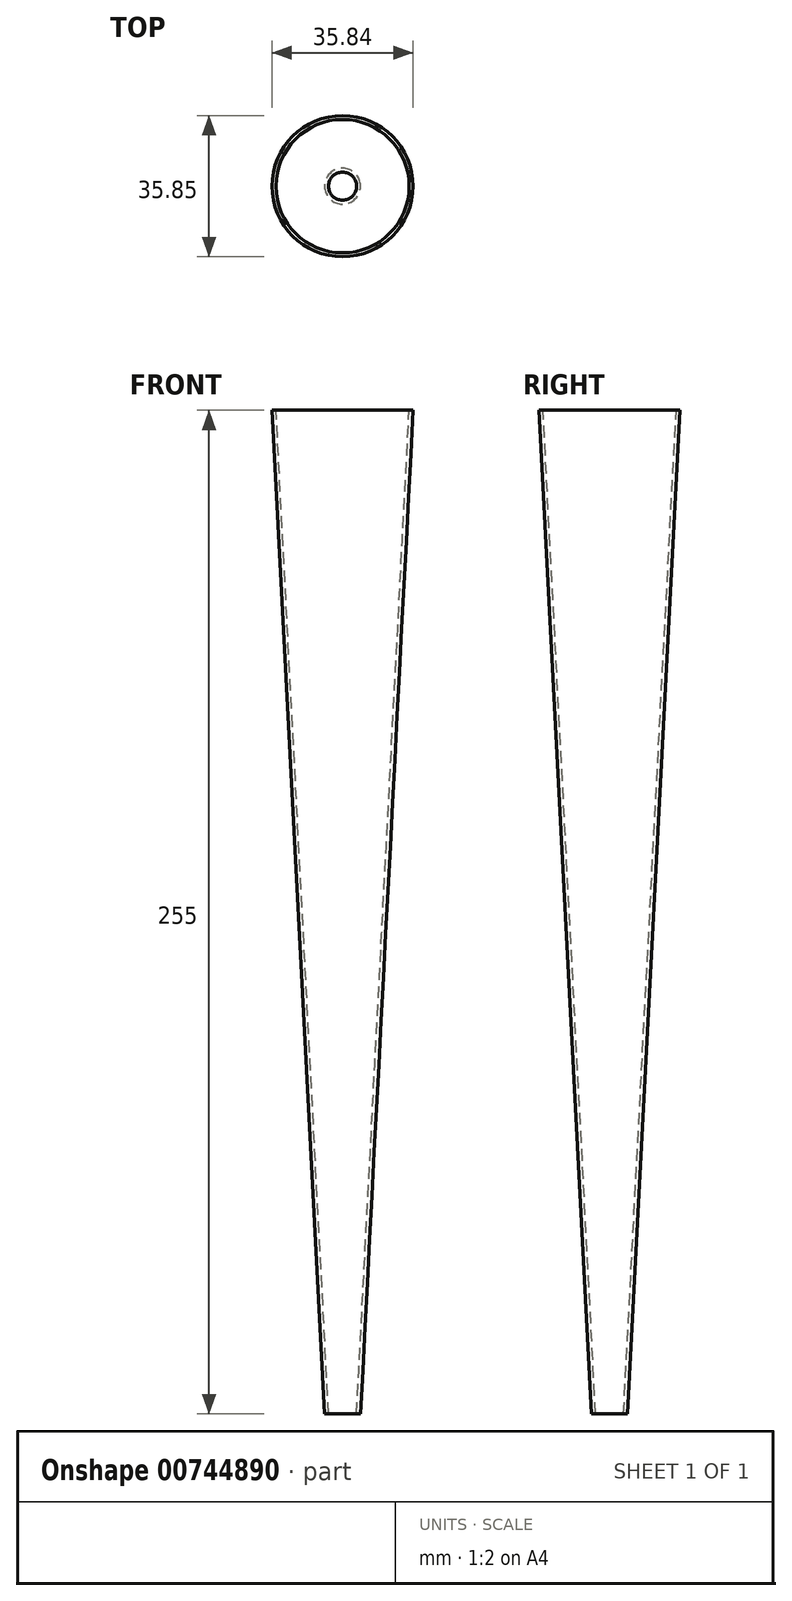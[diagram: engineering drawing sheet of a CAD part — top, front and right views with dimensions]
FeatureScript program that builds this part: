
annotation { "Feature Type Name" : "Feature", "Feature Type Description" : "" }
export const myFeature = defineFeature(function(context is Context, id is Id, definition is map)
    precondition{}
    {
        {
            var Q0;
            Q0=qCreatedBy(makeId("Top.planeOp"),FACE);
            var sketch = newSketch(context, id + "F0", { "sketchPlane" : qUnion([Q0])});
            skFitSpline(sketch, "E0", {"points": [v(-89.31, -40.87) * mm, v(-55.28, -96.62) * mm, v(25.38, -104.28) * mm], "startDerivative": vector(-32.43, -176.36) * mm, "endDerivative": vector(179.34, 79.88) * mm});
            skLineSegment(sketch, "E1", {"start": v(70.92, 0) * mm, "end": v(-42.75, 0) * mm});
            skCircle(sketch, "E2", {"center": v(-31.1, 39.75) * mm, "radius": 17.92 * mm});
            skLineSegment(sketch, "E3", {"start": v(47.65, -29.7) * mm, "end": v(-31.1, -29.7) * mm});
            skLineSegment(sketch, "E4.bottom", {"start": v(21.3, 53.07) * mm, "end": v(52.3, 53.07) * mm});
            skLineSegment(sketch, "E4.top", {"start": v(16.3, 28.6) * mm, "end": v(52.3, 28.6) * mm});
            skLineSegment(sketch, "E4.left", {"start": v(16.3, 48.07) * mm, "end": v(16.3, 28.6) * mm});
            skLineSegment(sketch, "E4.right", {"start": v(0, 65.87) * mm, "end": v(0, 41.4) * mm});
            skLineSegment(sketch, "E5.bottom", {"start": v(-106.26, -27.96) * mm, "end": v(-129.95, -54.55) * mm});
            skLineSegment(sketch, "E5.top", {"start": v(-121.12, -15.7) * mm, "end": v(-145.38, -43.17) * mm});
            skLineSegment(sketch, "E5.left", {"start": v(-106.26, -27.96) * mm, "end": v(-121.12, -15.7) * mm});
            skLineSegment(sketch, "E5.right", {"start": v(-129.95, -54.55) * mm, "end": v(-145.38, -43.17) * mm});
            skFitSpline(sketch, "E6", {"points": [v(-101.97, 14.2) * mm, v(-89.31, -21.03) * mm, v(-79.18, -9.41) * mm, v(-106.53, 26.98) * mm, v(-69.44, 36.9) * mm, v(-73.67, 17.02) * mm], "startDerivative": vector(44.32, -220.57) * mm, "endDerivative": vector(-78.16, -144.23) * mm});
            skPoint(sketch, "E7.visualSharp", {"position": v(16.3, 53.07) * mm});
            skArc(sketch, "E7.filletArc", {"start": v(21.3, 53.07) * mm, "mid": v(17.76, 51.6) * mm, "end": v(16.3, 48.07) * mm});
            skFitSpline(sketch, "E8", {"points": [v(-105.8, 41.62) * mm, v(-141.5, 13.76) * mm, v(-143.51, -13.98) * mm], "startDerivative": vector(-67.24, 12.42) * mm, "endDerivative": vector(8.74, -68.77) * mm});
            skArc(sketch, "E9.filletArc", {"start": v(-148.86, 45.52) * mm, "mid": v(-140.48, 24.92) * mm, "end": v(-118.24, 24.8) * mm});
            skLineSegment(sketch, "E10", {"start": v(-88.13, -62.94) * mm, "end": v(-147.1, -81.72) * mm});
            skLineSegment(sketch, "E11", {"start": v(-147.1, -81.72) * mm, "end": v(-111.1, -128.85) * mm});
            skLineSegment(sketch, "E12", {"start": v(-107.4, -84.55) * mm, "end": v(-138.79, -64) * mm});
            skLineSegment(sketch, "E13", {"start": v(-83.1, -103.85) * mm, "end": v(-134.58, -30.94) * mm});
            skLineSegment(sketch, "E14", {"start": v(26.35, -16.53) * mm, "end": v(64, -16.53) * mm});
            skLineSegment(sketch, "E15", {"start": v(52.79, -48.5) * mm, "end": v(-72.6, -48.5) * mm});
            skLineSegment(sketch, "E16", {"start": v(31.5, -85.86) * mm, "end": v(81.27, -85.86) * mm});
            skArc(sketch, "E17.0.startCap", {"start": v(31.5, -90.86) * mm, "mid": v(26.5, -85.86) * mm, "end": v(31.5, -80.86) * mm});
            skArc(sketch, "E17.0.endCap", {"start": v(81.27, -80.86) * mm, "mid": v(86.27, -85.86) * mm, "end": v(81.27, -90.86) * mm});
            skLineSegment(sketch, "E17.0.left", {"start": v(31.5, -80.86) * mm, "end": v(81.27, -80.86) * mm});
            skLineSegment(sketch, "E17.0.right", {"start": v(-17.85, -156.94) * mm, "end": v(17.35, -121.74) * mm});
            skArc(sketch, "E17.1.startCap", {"start": v(52.79, -43.5) * mm, "mid": v(57.79, -48.5) * mm, "end": v(52.79, -53.5) * mm});
            skArc(sketch, "E17.1.endCap", {"start": v(-72.6, -53.5) * mm, "mid": v(-77.6, -48.5) * mm, "end": v(-72.6, -43.5) * mm});
            skLineSegment(sketch, "E17.1.left", {"start": v(52.79, -53.5) * mm, "end": v(-72.6, -53.5) * mm});
            skLineSegment(sketch, "E17.1.right", {"start": v(52.79, -43.5) * mm, "end": v(-72.6, -43.5) * mm});
            skArc(sketch, "E17.2.startCap", {"start": v(26.35, -21.53) * mm, "mid": v(21.35, -16.53) * mm, "end": v(26.35, -11.53) * mm});
            skArc(sketch, "E17.2.endCap", {"start": v(64, -11.53) * mm, "mid": v(69, -16.53) * mm, "end": v(64, -21.53) * mm});
            skLineSegment(sketch, "E17.2.left", {"start": v(26.35, -11.53) * mm, "end": v(64, -11.53) * mm});
            skLineSegment(sketch, "E17.2.right", {"start": v(26.35, -21.53) * mm, "end": v(64, -21.53) * mm});
            skSolve(sketch);
        }
        {
            var Q0;
            Q0=makeQuery(id+"F0.imprint","IMPRINT",FACE,{"disambiguationData":[TD([[makeQuery(id+"F0.imprint","IMPRINT",EDGE,{"derivedFrom":sQuery(id+"F0.wireOp",EDGE,"E2")}),1.0]])]});
            extrude(context, id + "F1", {"entities" : qUnion([Q0]), "oppositeDirection" : true, "depth" : 255 * mm, "offsetDistance" : 25 * mm, "hasDraft" : true, "draftAngle" : 3 * degree, "draftPullDirection" : true, "hasSecondDirectionDraft" : true, "secondDirectionDraftAngle" : 3 * degree});
        }
        {
            var Q0;
            Q0=makeQuery(id+"F1.opExtrude","CAP_FACE",FACE,{"disambiguationData":[OSD([sQuery(id+"F0.wireOp",EDGE,"E2")])],"isStart":true});
            var Q1;
            Q1=makeQuery(id+"F1.opExtrude","CAP_FACE",FACE,{"disambiguationData":[OSD([sQuery(id+"F0.wireOp",EDGE,"E2")])],"isStart":false});
            var Q2;
            Q2=makeQuery(id+"F1.opExtrude","SWEPT_BODY",BODY,{"disambiguationData":[OSD([sQuery(id+"F0.wireOp",EDGE,"E2")])]});
            shell(context, id + "F2", {"entities" : qUnion([Q0, Q1]), "parts" : qUnion([Q2]), "thickness" : 1 * mm});
        }
    });
